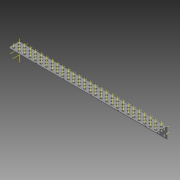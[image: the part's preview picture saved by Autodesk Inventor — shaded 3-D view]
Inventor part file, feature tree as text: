
AUTODESK INVENTOR PART (.ipt)
format: ipt  version: 2015 (Build 190159000, 159)  size: 2,249,216 bytes
history: native  units: in
note: dims shown in document units (in); Inventor stores cm internally (conversion verified against a paired STEP export)
features: other x167, pattern_linear x4, sheet_metal_op x1, extrude x1, imported_body x1, sketch x1
ambient origin geometry x8: Origin, YZ Plane, XZ Plane, XY Plane, X Axis, Y Axis, Z Axis, Center Point
bodies: Body1 (feature_tree)
feature tree (175):
  sheet_metal_op  "Fold1"
  other  "L-Channel"
  extrude  "length cut"  Depth=0.5in
  other  "top out axis"
  other  "top inner axis"
  other  "back out axis"
  other  "back inner axis"
  pattern_linear  "top outer axes"  Count1=2 Spacing1=0.5in
  pattern_linear  "top inner axes"  Spacing1=0.5in  [1 undecoded]
  pattern_linear  "back outer axes"  Count1=2 Spacing1=0.5in
  pattern_linear  "back inner axes"  Spacing1=0.5in  [1 undecoded]
  other  "right plane"
  imported_body  "Base1"
  sketch  "Sketch1"  dims[d1=0.0in d4=0.5in d5=0.7874in d7=0.5in d10=0.5in d13=0.5in d14=0.7874in d16=0.5in d19=0.5in d20=-13.5in d21=0.0in d22=0.0in d23=0.0in d24=0.0in d25=0.0in d26=0.0in]
  other  "Work Point1"
  other  "Work Point2"
  other  "Work Point3"
  other  "Work Point4"
  other  "Work Axis5"
  other  "Work Axis6"
  other  "Work Axis7"
  other  "Work Axis8"
  other  "Work Axis11"
  other  "Work Axis12"
  other  "Work Axis13"
  other  "Work Axis14"
  other  "Work Axis15"
  other  "Work Axis18"
  other  "Work Axis19"
  other  "Work Axis20"
  other  "Work Axis23"
  other  "Work Axis24"
  other  "Work Axis25"
  other  "Work Axis26"
  other  "Work Axis29"
  other  "Work Axis30"
  other  "Work Axis31"
  other  "Work Axis32"
  other  "Work Axis33"
  other  "Work Axis36"
  other  "Work Axis37"
  other  "Work Axis38"
  other  "Work Axis41"
  other  "Work Axis42"
  other  "Work Axis43"
  other  "Work Axis44"
  other  "Work Axis45"
  other  "Work Axis46"
  other  "Work Axis47"
  other  "Work Axis48"
  other  "Work Axis49"
  other  "Work Axis50"
  other  "Work Axis51"
  other  "Work Axis52"
  other  "Work Axis53"
  other  "Work Axis54"
  other  "Work Axis55"
  other  "Work Axis56"
  other  "Work Axis57"
  other  "Work Axis58"
  other  "Work Axis59"
  other  "Work Axis60"
  other  "Work Axis61"
  other  "Work Axis62"
  other  "Work Axis63"
  other  "Work Axis64"
  other  "Work Axis65"
  other  "Work Axis66"
  other  "Work Axis67"
  other  "Work Axis68"
  other  "Work Axis69"
  other  "Work Axis70"
  other  "Work Axis71"
  other  "Work Axis72"
  other  "Work Axis73"
  other  "Work Axis74"
  other  "Work Axis75"
  other  "Work Axis76"
  other  "Work Axis77"
  other  "Work Axis78"
  other  "Work Axis79"
  other  "Work Axis80"
  other  "Work Axis81"
  other  "Work Axis82"
  other  "Work Axis83"
  other  "Work Axis84"
  other  "Work Axis85"
  other  "Work Axis86"
  other  "Work Axis87"
  other  "Work Axis88"
  other  "Work Axis89"
  other  "Work Axis90"
  other  "Work Axis91"
  other  "Work Axis92"
  other  "Work Axis93"
  other  "Work Axis94"
  other  "Work Axis95"
  other  "Work Axis96"
  other  "Work Axis97"
  other  "Work Axis98"
  other  "Work Axis99"
  other  "Work Axis100"
  other  "Work Axis101"
  other  "Work Axis102"
  other  "Work Axis103"
  other  "Work Axis104"
  other  "Work Axis105"
  other  "Work Axis106"
  other  "Work Axis107"
  other  "Work Axis108"
  other  "Work Axis109"
  other  "Work Axis110"
  other  "Work Axis111"
  other  "Work Axis112"
  other  "Work Axis113"
  other  "Work Axis114"
  other  "Work Axis115"
  other  "Work Axis116"
  other  "Work Axis117"
  other  "Work Axis118"
  other  "Work Axis119"
  other  "Work Axis120"
  other  "Work Axis121"
  other  "Work Axis122"
  other  "Work Axis123"
  other  "Work Axis124"
  other  "Work Axis125"
  other  "Work Axis126"
  other  "Work Axis127"
  other  "Work Axis128"
  other  "Work Axis129"
  other  "Work Axis130"
  other  "Work Axis131"
  other  "Work Axis132"
  other  "Work Axis133"
  other  "Work Axis134"
  other  "Work Axis135"
  other  "Work Axis136"
  other  "Work Axis137"
  other  "Work Axis138"
  other  "Work Axis139"
  other  "Work Axis140"
  other  "Work Axis141"
  other  "Work Axis142"
  other  "Work Axis143"
  other  "Work Axis144"
  other  "Work Axis145"
  other  "Work Axis146"
  other  "Work Axis147"
  other  "Work Axis148"
  other  "Work Axis149"
  other  "Work Axis150"
  other  "Work Axis151"
  other  "Work Axis152"
  other  "Work Axis153"
  other  "Work Axis154"
  other  "Work Axis155"
  other  "Work Axis156"
  other  "Work Axis157"
  other  "Work Axis158"
  other  "Work Axis159"
  other  "Work Axis160"
  other  "left plane"
  other  "Work Axis161"
  other  "Work Axis162"
  other  "Work Axis164"
  other  "Work Axis165"
  other  "Work Axis167"
  other  "Work Axis168"
  other  "Work Axis170"
  other  "Work Axis171"
  other  "Work Axis173"
  other  "Work Axis174"
  other  "Work Axis176"
  other  "Work Axis177"
note: 2 required parameter values undecoded (feature->parameter linkage not recoverable at this tier; creation-order binding heuristic only, values carry confidence <= 0.55)
